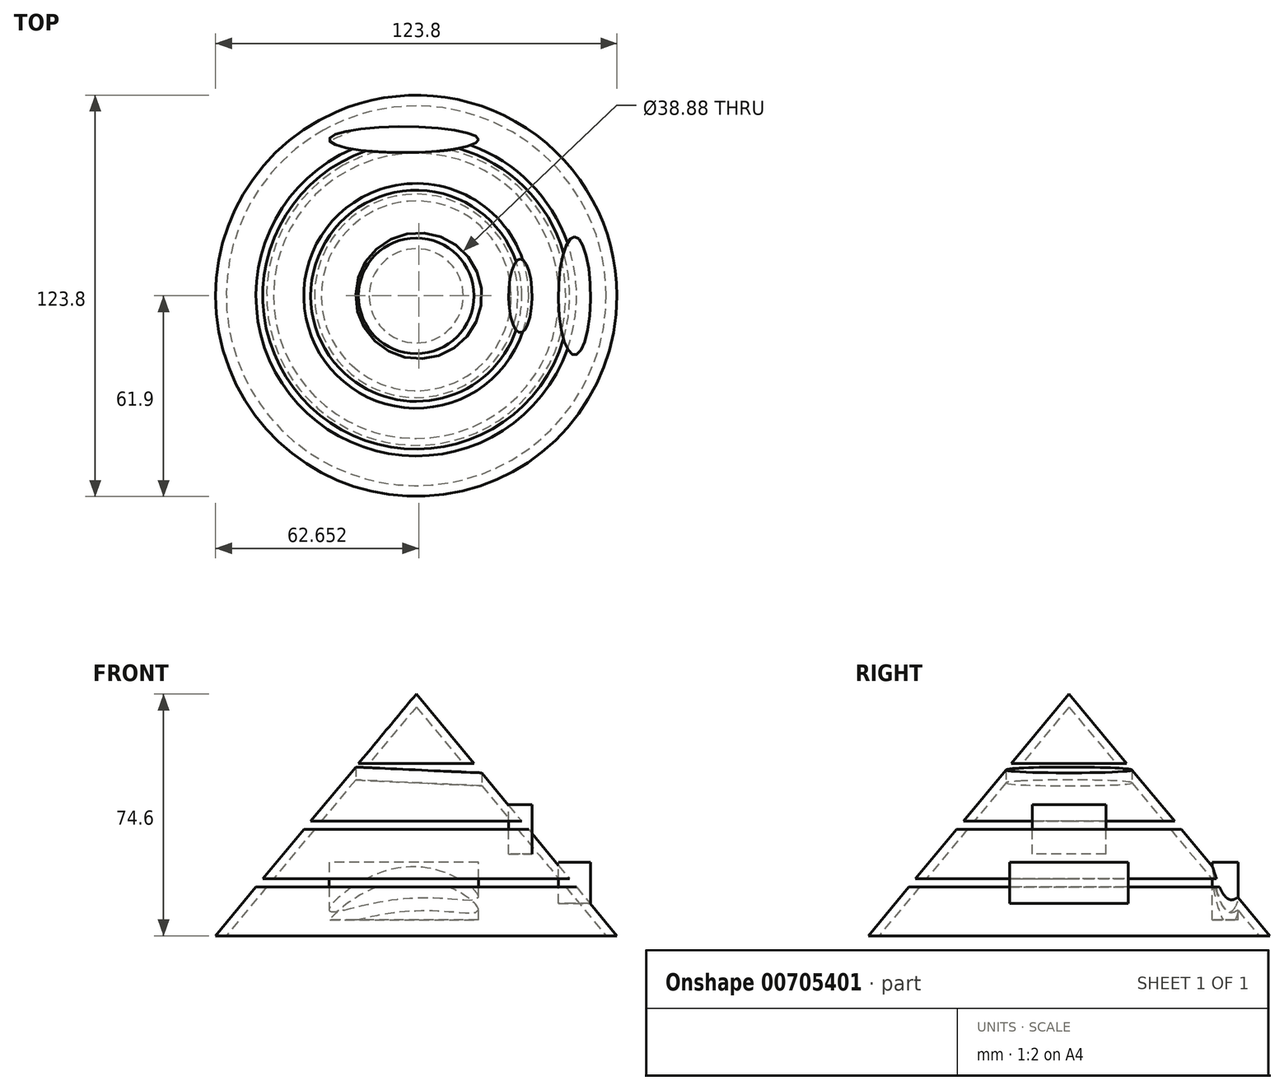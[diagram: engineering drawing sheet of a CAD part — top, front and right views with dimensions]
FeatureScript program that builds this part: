
annotation { "Feature Type Name" : "Feature", "Feature Type Description" : "" }
export const myFeature = defineFeature(function(context is Context, id is Id, definition is map)
    precondition{}
    {
        {
            var Q0;
            Q0=qCreatedBy(makeId("Front.planeOp"),FACE);
            var sketch = newSketch(context, id + "F0", { "sketchPlane" : qUnion([Q0])});
            skLineSegment(sketch, "E0", {"start": v(-32.1, 39.26) * mm, "end": v(-32.1, -35.34) * mm});
            skLineSegment(sketch, "E1", {"start": v(-32.1, -35.34) * mm, "end": v(29.8, -35.34) * mm});
            skLineSegment(sketch, "E2", {"start": v(29.8, -35.34) * mm, "end": v(-32.1, 39.26) * mm});
            skSolve(sketch);
        }
        {
            var Q0;
            Q0=makeQuery(id+"F0.imprint","IMPRINT",FACE,{"disambiguationData":[TD([[makeQuery(id+"F0.imprint","IMPRINT",EDGE,{"derivedFrom":sQuery(id+"F0.wireOp",EDGE,"E0")}),1.0]])]});
            var Q1;
            Q1=sQuery(id+"F0.wireOp",EDGE,"E0");
            revolve(context, id + "F1", {"surfaceOperationType" : NewSurfaceOperationType.NEW, "entities" : qUnion([Q0]), "axis" : qUnion([Q1]), "revolveType" : RevolveType.FULL});
        }
        {
            var Q0;
            Q0=makeQuery(id+"F1.opRevolve","SWEPT_FACE",FACE,{"disambiguationData":[OSD([sQuery(id+"F0.wireOp",EDGE,"E1")])]});
            shell(context, id + "F2", {"entities" : qUnion([Q0]), "thickness" : 2.54 * mm});
        }
        {
            var Q0;
            Q0=qCreatedBy(makeId("Top.planeOp"),FACE);
            var sketch = newSketch(context, id + "F3", { "sketchPlane" : qUnion([Q0])});
            skCircle(sketch, "E3", {"center": v(-31.9, 0) * mm, "radius": 62.39 * mm});
            skSolve(sketch);
        }
        {
            var Q0;
            Q0=makeQuery(id+"F3.imprint","IMPRINT",FACE,{"disambiguationData":[TD([[makeQuery(id+"F3.imprint","IMPRINT",EDGE,{"derivedFrom":sQuery(id+"F3.wireOp",EDGE,"E3")}),1.0]])]});
            extrude(context, id + "F4", {"entities" : qUnion([Q0]), "operationType" : NewBodyOperationType.REMOVE, "oppositeDirection" : true, "depth" : 2.54 * mm, "offsetDistance" : 25.4 * mm});
        }
        {
            var Q0;
            Q0=qCreatedBy(makeId("Top.planeOp"),FACE);
            var sketch = newSketch(context, id + "F5", { "sketchPlane" : qUnion([Q0])});
            skCircle(sketch, "E4", {"center": v(-31.35, 0) * mm, "radius": 19.44 * mm});
            skSolve(sketch);
        }
        {
            var Q0;
            Q0=makeQuery(id+"F5.imprint","IMPRINT",FACE,{"disambiguationData":[TD([[makeQuery(id+"F5.imprint","IMPRINT",EDGE,{"derivedFrom":sQuery(id+"F5.wireOp",EDGE,"E4")}),1.0]])]});
            var Q1;
            Q1=sQuery(id+"F5.wireOp",EDGE,"E4");
            extrude(context, id + "F6", {"entities" : qUnion([Q0]), "operationType" : NewBodyOperationType.REMOVE, "surfaceEntities" : qUnion([Q1]), "depth" : 17.78 * mm, "offsetDistance" : 25.4 * mm, "hasSecondDirection" : true, "secondDirectionOppositeDirection" : true, "secondDirectionDepth" : 5.08 * mm});
        }
        {
            var Q0;
            Q0=qCreatedBy(makeId("Top.planeOp"),FACE);
            var sketch = newSketch(context, id + "F7", { "sketchPlane" : qUnion([Q0])});
            skCircle(sketch, "E5", {"center": v(-31.85, 0) * mm, "radius": 51.42 * mm});
            skSolve(sketch);
        }
        {
            var Q0;
            Q0=makeQuery(id+"F7.imprint","IMPRINT",FACE,{"disambiguationData":[TD([[makeQuery(id+"F7.imprint","IMPRINT",EDGE,{"derivedFrom":sQuery(id+"F7.wireOp",EDGE,"E5")}),1.0]])]});
            extrude(context, id + "F8", {"entities" : qUnion([Q0]), "operationType" : NewBodyOperationType.REMOVE, "oppositeDirection" : true, "depth" : 20.32 * mm, "offsetDistance" : 25.4 * mm, "hasSecondDirection" : true, "secondDirectionOppositeDirection" : false, "secondDirectionDepth" : -17.78 * mm});
        }
        {
            var Q0;
            Q0=qCreatedBy(makeId("Top.planeOp"),FACE);
            var sketch = newSketch(context, id + "F9", { "sketchPlane" : qUnion([Q0])});
            skEllipse(sketch, "E6", {"center": v(0, 0) * mm, "majorRadius": 11.37 * mm, "minorRadius": 3.6 * mm, "majorAxis": v(0, 1)});
            skSolve(sketch);
        }
        {
            var Q0;
            Q0=makeQuery(id+"F9.imprint","IMPRINT",FACE,{"disambiguationData":[TD([[makeQuery(id+"F9.imprint","IMPRINT",EDGE,{"derivedFrom":sQuery(id+"F9.wireOp",EDGE,"E6")}),1.0]])]});
            var Q1;
            Q1=sQuery(id+"F9.wireOp",EDGE,"E6");
            extrude(context, id + "F10", {"entities" : qUnion([Q0]), "surfaceEntities" : qUnion([Q1]), "oppositeDirection" : true, "depth" : 10.16 * mm, "offsetDistance" : 25.4 * mm, "hasSecondDirection" : true, "secondDirectionOppositeDirection" : false, "secondDirectionDepth" : 5.08 * mm});
        }
        {
            var Q0;
            Q0=qCreatedBy(makeId("Top.planeOp"),FACE);
            var sketch = newSketch(context, id + "F11", { "sketchPlane" : qUnion([Q0])});
            skEllipse(sketch, "E7", {"center": v(-35.95, 48.2) * mm, "majorRadius": 23.02 * mm, "minorRadius": 4 * mm, "majorAxis": v(1, 0)});
            skSolve(sketch);
        }
        {
            var Q0;
            Q0=makeQuery(id+"F11.imprint","IMPRINT",FACE,{"disambiguationData":[TD([[makeQuery(id+"F11.imprint","IMPRINT",EDGE,{"derivedFrom":sQuery(id+"F11.wireOp",EDGE,"E7")}),1.0]])]});
            var Q1;
            Q1=sQuery(id+"F11.wireOp",EDGE,"E7");
            extrude(context, id + "F12", {"entities" : qUnion([Q0]), "operationType" : NewBodyOperationType.ADD, "surfaceEntities" : qUnion([Q1]), "oppositeDirection" : true, "depth" : 30.48 * mm, "offsetDistance" : 25.4 * mm, "hasSecondDirection" : true, "secondDirectionOppositeDirection" : false, "secondDirectionDepth" : -12.7 * mm});
        }
        {
            var Q0;
            Q0=qCreatedBy(makeId("Top.planeOp"),FACE);
            var sketch = newSketch(context, id + "F13", { "sketchPlane" : qUnion([Q0])});
            skEllipse(sketch, "E8", {"center": v(-31.35, -48.2) * mm, "majorRadius": 21.87 * mm, "minorRadius": 4.06 * mm, "majorAxis": v(-1, 0)});
            skSolve(sketch);
        }
        {
            var Q0;
            Q0=qCreatedBy(makeId("Top.planeOp"),FACE);
            var sketch = newSketch(context, id + "F14", { "sketchPlane" : qUnion([Q0])});
            skEllipse(sketch, "E9", {"center": v(16.72, 0) * mm, "majorRadius": 18.28 * mm, "minorRadius": 4.94 * mm, "majorAxis": v(0, 1)});
            skSolve(sketch);
        }
        {
            var Q0;
            Q0=makeQuery(id+"F14.imprint","IMPRINT",FACE,{"disambiguationData":[TD([[makeQuery(id+"F14.imprint","IMPRINT",EDGE,{"derivedFrom":sQuery(id+"F14.wireOp",EDGE,"E9")}),1.0]])]});
            var Q1;
            Q1=sQuery(id+"F14.wireOp",EDGE,"E9");
            extrude(context, id + "F15", {"entities" : qUnion([Q0]), "surfaceEntities" : qUnion([Q1]), "oppositeDirection" : true, "depth" : 25.4 * mm, "offsetDistance" : 25.4 * mm, "hasSecondDirection" : true, "secondDirectionOppositeDirection" : false, "secondDirectionDepth" : -12.7 * mm});
        }
        {
            var Q0;
            Q0=sQuery(id+"F13.wireOp",EDGE,"E8");
            extrude(context, id + "F16", {"bodyType" : ToolBodyType.SURFACE, "surfaceEntities" : qUnion([Q0]), "oppositeDirection" : true, "depth" : 33.02 * mm, "offsetDistance" : 25.4 * mm, "hasSecondDirection" : true, "secondDirectionOppositeDirection" : false, "secondDirectionDepth" : -12.7 * mm});
        }
        {
            var Q0;
            Q0=qCreatedBy(makeId("Top.planeOp"),FACE);
            var sketch = newSketch(context, id + "F17", { "sketchPlane" : qUnion([Q0])});
            skCircle(sketch, "E10", {"center": v(-31.95, 0) * mm, "radius": 18.53 * mm});
            skSolve(sketch);
        }
        {
            var Q0;
            Q0=sQuery(id+"F17.wireOp",EDGE,"E10");
            extrude(context, id + "F18", {"bodyType" : ToolBodyType.SURFACE, "surfaceEntities" : qUnion([Q0]), "depth" : 25.4 * mm, "offsetDistance" : 25.4 * mm});
        }
    });
